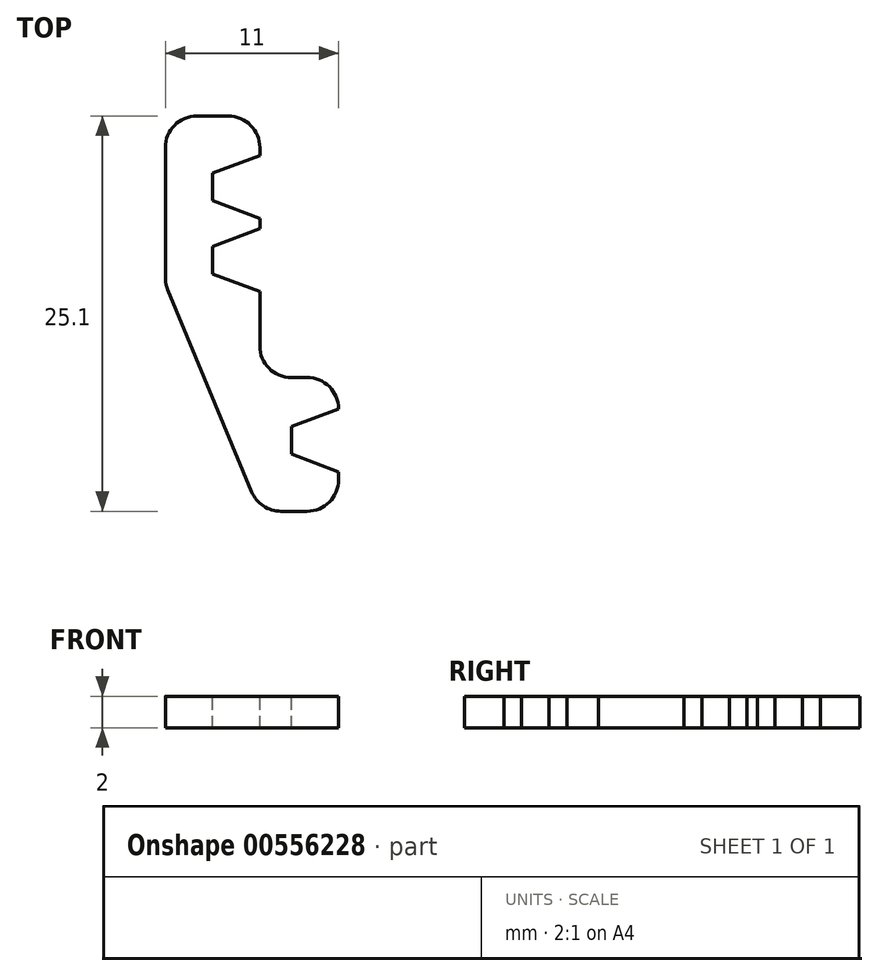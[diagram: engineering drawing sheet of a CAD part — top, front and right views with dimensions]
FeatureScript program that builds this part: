
annotation { "Feature Type Name" : "Feature", "Feature Type Description" : "" }
export const myFeature = defineFeature(function(context is Context, id is Id, definition is map)
    precondition{}
    {
        {
            var Q0;
            Q0=qCreatedBy(makeId("Top.planeOp"),FACE);
            var sketch = newSketch(context, id + "F0", { "sketchPlane" : qUnion([Q0])});
            skLineSegment(sketch, "E0", {"start": v(-14.2, 10.65) * mm, "end": v(-8.2, 10.65) * mm});
            skLineSegment(sketch, "E1", {"start": v(-8.2, 10.65) * mm, "end": v(-8.2, 6.65) * mm});
            skLineSegment(sketch, "E2", {"start": v(-8.2, 6.65) * mm, "end": v(-11.2, 6.65) * mm});
            skLineSegment(sketch, "E3", {"start": v(-11.2, 6.65) * mm, "end": v(-11.2, 5.65) * mm});
            skLineSegment(sketch, "E4", {"start": v(-11.2, 5.65) * mm, "end": v(-8.2, 5.65) * mm});
            skLineSegment(sketch, "E5", {"start": v(-8.2, 2) * mm, "end": v(-11.2, 2) * mm});
            skLineSegment(sketch, "E6", {"start": v(-11.2, 2) * mm, "end": v(-11.2, 1) * mm});
            skLineSegment(sketch, "E7", {"start": v(-11.2, 1) * mm, "end": v(-8.2, 1) * mm});
            skLineSegment(sketch, "E8", {"start": v(-3.2, -9.45) * mm, "end": v(-6.2, -9.45) * mm});
            skLineSegment(sketch, "E9", {"start": v(-6.2, -9.45) * mm, "end": v(-6.2, -10.45) * mm});
            skLineSegment(sketch, "E10", {"start": v(-6.2, -10.45) * mm, "end": v(-3.2, -10.45) * mm});
            skLineSegment(sketch, "E11", {"start": v(-3.2, -10.45) * mm, "end": v(-3.2, -14.45) * mm});
            skLineSegment(sketch, "E12", {"start": v(-3.2, -14.45) * mm, "end": v(-8.2, -14.45) * mm});
            skLineSegment(sketch, "E13", {"start": v(0, 15) * mm, "end": v(0, -15) * mm});
            skLineSegment(sketch, "E14", {"start": v(-8.2, 2) * mm, "end": v(-8.2, 5.65) * mm});
            skLineSegment(sketch, "E15", {"start": v(-14.2, 10.65) * mm, "end": v(-14.2, 0) * mm});
            skLineSegment(sketch, "E16", {"start": v(-14.2, 0) * mm, "end": v(-8.2, -14.45) * mm});
            skLineSegment(sketch, "E17", {"start": v(-3.2, -9.45) * mm, "end": v(-3.2, -5.95) * mm});
            skLineSegment(sketch, "E18", {"start": v(-3.2, -5.95) * mm, "end": v(-8.2, -5.95) * mm});
            skLineSegment(sketch, "E19", {"start": v(-8.2, 1) * mm, "end": v(-8.2, -5.95) * mm});
            skSolve(sketch);
        }
        {
            var Q0;
            Q0=makeQuery(id+"F0.imprint","IMPRINT",FACE,{"disambiguationData":[TD([[makeQuery(id+"F0.imprint","IMPRINT",EDGE,{"derivedFrom":sQuery(id+"F0.wireOp",EDGE,"E0")}),-1.0]])]});
            extrude(context, id + "F1", {"entities" : qUnion([Q0]), "depth" : 2 * mm, "offsetDistance" : 25 * mm});
        }
        {
            var Q0;
            Q0=makeQuery(id+"F1.opExtrude","SWEPT_EDGE",EDGE,{"disambiguationData":[OSD([sQuery(id+"F0.wireOp",EDGE,"E0"),sQuery(id+"F0.wireOp",EDGE,"E15")])]});
            var Q1;
            Q1=makeQuery(id+"F1.opExtrude","SWEPT_EDGE",EDGE,{"disambiguationData":[OSD([sQuery(id+"F0.wireOp",EDGE,"E15"),sQuery(id+"F0.wireOp",EDGE,"E16")])]});
            var Q2;
            Q2=makeQuery(id+"F1.opExtrude","SWEPT_EDGE",EDGE,{"disambiguationData":[OSD([sQuery(id+"F0.wireOp",EDGE,"E0"),sQuery(id+"F0.wireOp",EDGE,"E1")])]});
            var Q3;
            Q3=makeQuery(id+"F1.opExtrude","SWEPT_EDGE",EDGE,{"disambiguationData":[OSD([sQuery(id+"F0.wireOp",EDGE,"E12"),sQuery(id+"F0.wireOp",EDGE,"E16")])]});
            var Q4;
            Q4=makeQuery(id+"F1.opExtrude","SWEPT_EDGE",EDGE,{"disambiguationData":[OSD([sQuery(id+"F0.wireOp",EDGE,"E11"),sQuery(id+"F0.wireOp",EDGE,"E12")])]});
            var Q5;
            Q5=makeQuery(id+"F1.opExtrude","SWEPT_EDGE",EDGE,{"disambiguationData":[OSD([sQuery(id+"F0.wireOp",EDGE,"E17"),sQuery(id+"F0.wireOp",EDGE,"E18")])]});
            fillet(context, id + "F2", {"entities" : qUnion([Q0, Q1, Q2, Q3, Q4, Q5]), "radius" : 2 * mm, "tangentPropagation" : true, "allowEdgeOverflow" : false});
        }
        {
            var Q0;
            Q0=makeQuery(id+"F1.opExtrude","SWEPT_EDGE",EDGE,{"disambiguationData":[OSD([sQuery(id+"F0.wireOp",EDGE,"E18"),sQuery(id+"F0.wireOp",EDGE,"E19")])]});
            fillet(context, id + "F3", {"entities" : qUnion([Q0]), "radius" : 2 * mm, "tangentPropagation" : true, "allowEdgeOverflow" : false});
        }
        {
            var Q0;
            Q0=makeQuery(id+"F1.opExtrude","SWEPT_EDGE",EDGE,{"disambiguationData":[OSD([sQuery(id+"F0.wireOp",EDGE,"E1"),sQuery(id+"F0.wireOp",EDGE,"E2")])]});
            var Q1;
            Q1=makeQuery(id+"F1.opExtrude","SWEPT_EDGE",EDGE,{"disambiguationData":[OSD([sQuery(id+"F0.wireOp",EDGE,"E5"),sQuery(id+"F0.wireOp",EDGE,"E14")])]});
            var Q2;
            Q2=makeQuery(id+"F1.opExtrude","SWEPT_EDGE",EDGE,{"disambiguationData":[OSD([sQuery(id+"F0.wireOp",EDGE,"E8"),sQuery(id+"F0.wireOp",EDGE,"E17")])]});
            chamfer(context, id + "F4", {"entities" : qUnion([Q0, Q1, Q2]), "chamferType" : ChamferType.TWO_OFFSETS, "width1" : 1.5 * mm, "oppositeDirection" : false, "width2" : 4 * mm, "tangentPropagation" : true});
        }
        {
            var Q0;
            Q0=makeQuery(id+"F1.opExtrude","SWEPT_EDGE",EDGE,{"disambiguationData":[OSD([sQuery(id+"F0.wireOp",EDGE,"E4"),sQuery(id+"F0.wireOp",EDGE,"E14")])]});
            var Q1;
            Q1=makeQuery(id+"F1.opExtrude","SWEPT_EDGE",EDGE,{"disambiguationData":[OSD([sQuery(id+"F0.wireOp",EDGE,"E10"),sQuery(id+"F0.wireOp",EDGE,"E11")])]});
            chamfer(context, id + "F5", {"entities" : qUnion([Q0, Q1]), "chamferType" : ChamferType.TWO_OFFSETS, "width1" : 4 * mm, "oppositeDirection" : false, "width2" : 1.5 * mm, "tangentPropagation" : true});
        }
        {
            var Q0;
            Q0=makeQuery(id+"F1.opExtrude","SWEPT_EDGE",EDGE,{"disambiguationData":[OSD([sQuery(id+"F0.wireOp",EDGE,"E7"),sQuery(id+"F0.wireOp",EDGE,"E19")])]});
            chamfer(context, id + "F6", {"entities" : qUnion([Q0]), "chamferType" : ChamferType.TWO_OFFSETS, "width1" : 4 * mm, "oppositeDirection" : false, "width2" : 1.5 * mm, "tangentPropagation" : true});
        }
    });
